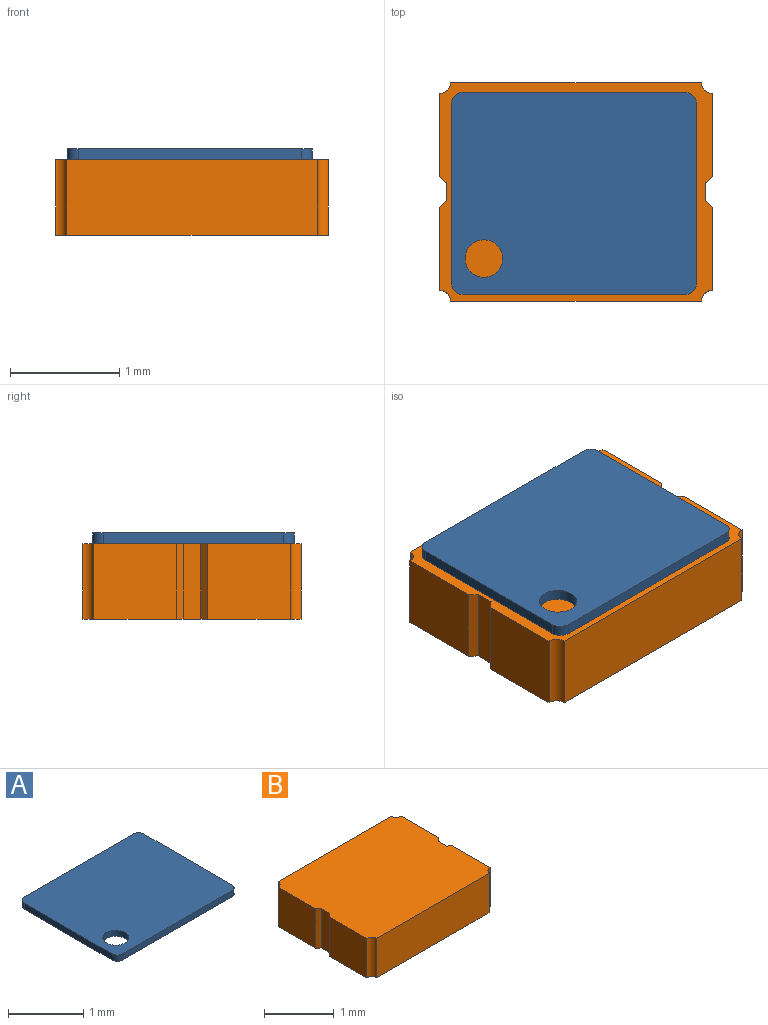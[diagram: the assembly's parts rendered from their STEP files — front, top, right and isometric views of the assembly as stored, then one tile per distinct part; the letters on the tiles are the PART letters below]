
ASSEMBLY  parts=2 mates=1
PART A: 11 faces, bbox 2.2x1.8x0.1 mm
  f0: cylinder r=0.17mm len=0.34mm, axis (0,0,-1), area 0.1mm2, adj f1,f10
  f1: plane 2.25x1.85mm, normal (0,0,-1), area 4.1mm2, adj f0,f2,f3,f4,f5,f6,f7,f8
  f2: plane 1.65x0.1mm, normal (1,0,0), area 0.2mm2, adj f1,f3,f9,f10
  f3: cylinder r=0.1mm len=0.1mm, axis (0,0,-1), area 0mm2, adj f1,f2,f4,f10
  f4: plane 2.05x0.1mm, normal (0,-1,0), area 0.2mm2, adj f1,f3,f5,f10
  f5: cylinder r=0.1mm len=0.1mm, axis (0,0,-1), area 0mm2, adj f1,f4,f6,f10
  f6: plane 1.65x0.1mm, normal (-1,0,0), area 0.2mm2, adj f1,f5,f7,f10
  f7: cylinder r=0.1mm len=0.1mm, axis (0,0,-1), area 0mm2, adj f1,f6,f8,f10
  f8: plane 2.05x0.1mm, normal (0,1,0), area 0.2mm2, adj f1,f7,f9,f10
  f9: cylinder r=0.1mm len=0.1mm, axis (0,0,-1), area 0mm2, adj f1,f2,f8,f10
  f10: plane 2.25x1.85mm, normal (0,0,1), area 4.1mm2, adj f0,f2,f3,f4,f5,f6,f7,f8
PART B: 18 faces, bbox 2.5x2x0.7 mm
  f0: plane 2.5x2mm, normal (0,0,1), area 4.9mm2, adj f1,f2,f3,f4,f5,f6,f7,f8
  f1: plane 0.69x0.07mm, normal (0.67,0.74,0), area 0.1mm2, adj f0,f2,f16,f17
  f2: plane 0.76x0.69mm, normal (1,0,0), area 0.5mm2, adj f0,f1,f3,f17
  f3: cylinder r=0.1mm len=0.69mm, axis (0,0,-1), area 0.1mm2, adj f0,f2,f4,f17
  f4: plane 2.3x0.69mm, normal (0,-1,0), area 1.6mm2, adj f0,f3,f5,f17
  f5: cylinder r=0.1mm len=0.69mm, axis (0,0,-1), area 0.1mm2, adj f0,f4,f6,f17
  f6: plane 0.76x0.69mm, normal (-1,0,0), area 0.5mm2, adj f0,f5,f7,f17
  f7: plane 0.69x0.07mm, normal (-0.67,0.74,0), area 0.1mm2, adj f0,f6,f8,f17
  f8: plane 0.69x0.16mm, normal (-1,0,0), area 0.1mm2, adj f0,f7,f9,f17
  f9: plane 0.69x0.07mm, normal (-0.67,-0.74,0), area 0.1mm2, adj f0,f8,f10,f17
  f10: plane 0.76x0.69mm, normal (-1,0,0), area 0.5mm2, adj f0,f9,f11,f17
  f11: cylinder r=0.1mm len=0.69mm, axis (0,0,-1), area 0.1mm2, adj f0,f10,f12,f17
  f12: plane 2.3x0.69mm, normal (0,1,0), area 1.6mm2, adj f0,f11,f13,f17
  f13: cylinder r=0.1mm len=0.69mm, axis (0,0,-1), area 0.1mm2, adj f0,f12,f14,f17
  f14: plane 0.76x0.69mm, normal (1,0,0), area 0.5mm2, adj f0,f13,f15,f17
  f15: plane 0.69x0.07mm, normal (0.67,-0.74,0), area 0.1mm2, adj f0,f14,f16,f17
  f16: plane 0.69x0.16mm, normal (1,0,0), area 0.1mm2, adj f0,f1,f15,f17
  f17: plane 2.5x2mm, normal (0,0,-1), area 4.9mm2, adj f1,f2,f3,f4,f5,f6,f7,f8
PLACE A t=(-0.17,0.34,0.66)mm
PLACE B t=(-0.16,0.36,0.66)mm
MATE fastened B.f0 <-> A.f1  axis (0,0,1) through (-0.16,0.36,1.35)mm
